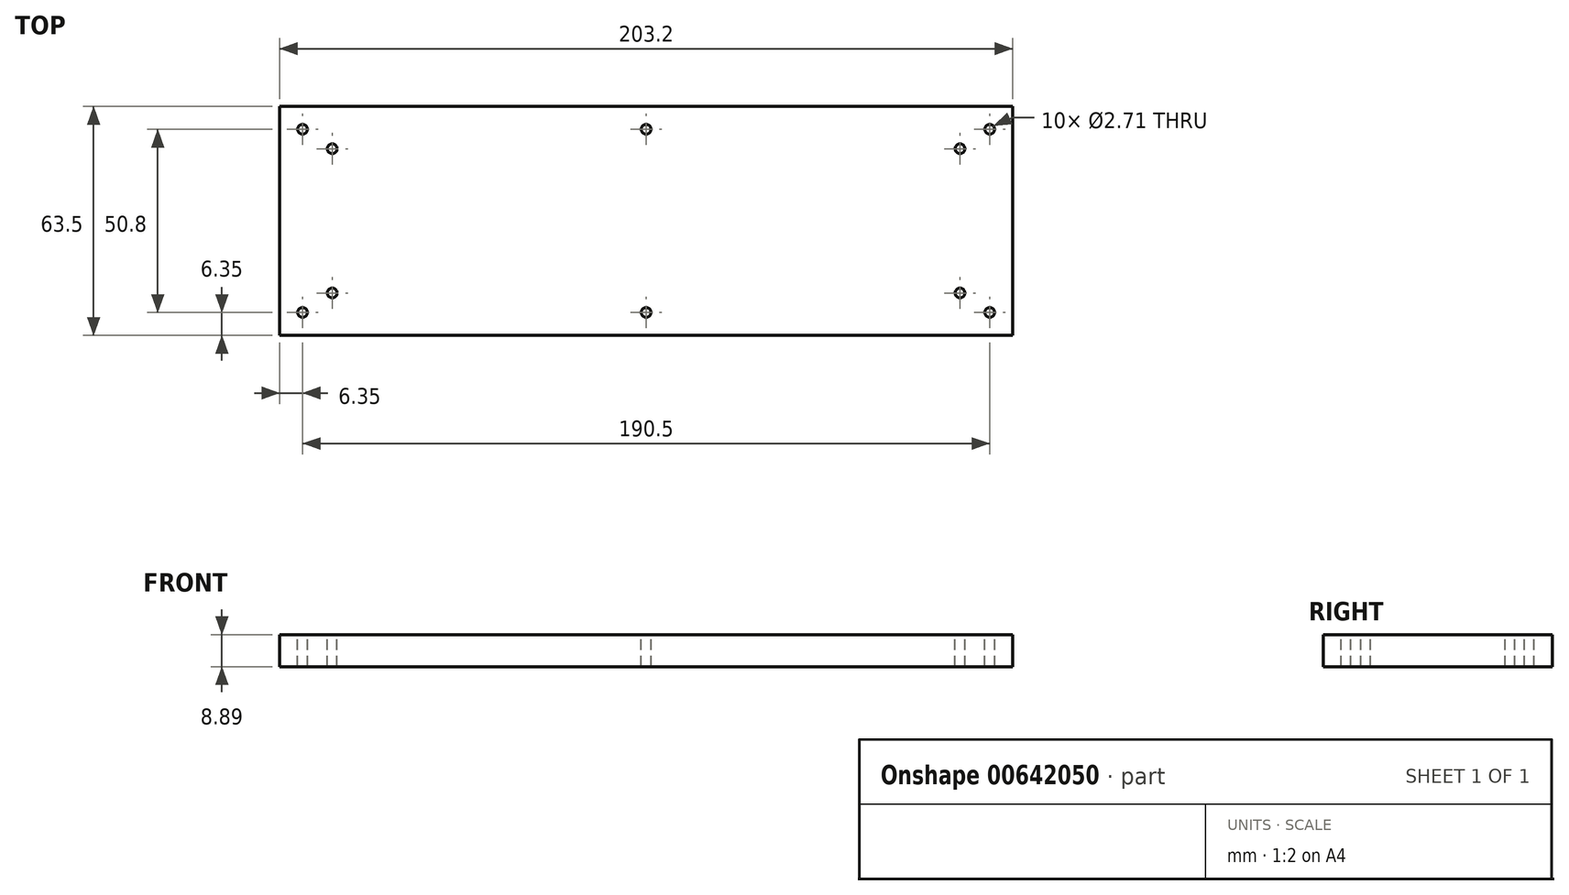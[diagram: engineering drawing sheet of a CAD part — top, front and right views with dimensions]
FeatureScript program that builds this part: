
annotation { "Feature Type Name" : "Feature", "Feature Type Description" : "" }
export const myFeature = defineFeature(function(context is Context, id is Id, definition is map)
    precondition{}
    {
        {
            var Q0;
            Q0=qCreatedBy(makeId("Top.planeOp"),FACE);
            var sketch = newSketch(context, id + "F0", { "sketchPlane" : qUnion([Q0])});
            skLineSegment(sketch, "E0.bottom", {"start": v(0, 0) * mm, "end": v(203.2, 0) * mm});
            skLineSegment(sketch, "E0.top", {"start": v(0, 63.5) * mm, "end": v(203.2, 63.5) * mm});
            skLineSegment(sketch, "E0.left", {"start": v(0, 0) * mm, "end": v(0, 63.5) * mm});
            skLineSegment(sketch, "E0.right", {"start": v(203.2, 0) * mm, "end": v(203.2, 63.5) * mm});
            skSolve(sketch);
        }
        {
            var Q0;
            Q0 = qSketchRegion(id + "F0", true);
            extrude(context, id + "F1", {"entities" : qUnion([Q0]), "depth" : 8.9 * mm, "offsetDistance" : 25.4 * mm});
        }
        {
            var Q0;
            Q0=makeQuery(id+"F1.opExtrude","CAP_FACE",FACE,{"disambiguationData":[OSD([sQuery(id+"F0.wireOp",EDGE,"E0.bottom"),sQuery(id+"F0.wireOp",EDGE,"E0.top"),sQuery(id+"F0.wireOp",EDGE,"E0.left"),sQuery(id+"F0.wireOp",EDGE,"E0.right")])],"isStart":false});
            var sketch = newSketch(context, id + "F2", { "sketchPlane" : qUnion([Q0])});
            skPoint(sketch, "E1", {"position": v(14.6, 51.75) * mm});
            skPoint(sketch, "E2", {"position": v(14.6, 11.75) * mm});
            skPoint(sketch, "E3", {"position": v(188.6, 51.75) * mm});
            skPoint(sketch, "E4", {"position": v(188.6, 11.75) * mm});
            skLineSegment(sketch, "E5", {"start": v(0, 31.75) * mm, "end": v(203.2, 31.75) * mm, "construction": true});
            skPoint(sketch, "E5.endSnap0", {"position": v(0, 31.75) * mm});
            skLineSegment(sketch, "E6", {"start": v(101.6, 63.5) * mm, "end": v(101.6, 0) * mm, "construction": true});
            skPoint(sketch, "E7", {"position": v(6.35, 57.15) * mm});
            skPoint(sketch, "E8", {"position": v(196.85, 57.15) * mm});
            skPoint(sketch, "E9", {"position": v(196.85, 6.35) * mm});
            skPoint(sketch, "E10", {"position": v(6.35, 6.35) * mm});
            skPoint(sketch, "E11", {"position": v(101.6, 57.15) * mm});
            skPoint(sketch, "E12", {"position": v(101.6, 6.35) * mm});
            skSolve(sketch);
        }
        {
            var Q0;
            Q0=sQuery(id+"F2.wireOp",VERTEX,"E8");
            var Q1;
            Q1=sQuery(id+"F2.wireOp",VERTEX,"E3");
            var Q2;
            Q2=sQuery(id+"F2.wireOp",VERTEX,"E4");
            var Q3;
            Q3=sQuery(id+"F2.wireOp",VERTEX,"E9");
            var Q4;
            Q4=sQuery(id+"F2.wireOp",VERTEX,"E10");
            var Q5;
            Q5=sQuery(id+"F2.wireOp",VERTEX,"E2");
            var Q6;
            Q6=sQuery(id+"F2.wireOp",VERTEX,"E1");
            var Q7;
            Q7=sQuery(id+"F2.wireOp",VERTEX,"E7");
            var Q8;
            Q8=sQuery(id+"F2.wireOp",VERTEX,"E11");
            var Q9;
            Q9=sQuery(id+"F2.wireOp",VERTEX,"E12");
            var Q10;
            Q10=makeQuery(id+"F1.opExtrude","SWEPT_BODY",BODY,{"disambiguationData":[OSD([sQuery(id+"F0.wireOp",EDGE,"E0.bottom"),sQuery(id+"F0.wireOp",EDGE,"E0.top"),sQuery(id+"F0.wireOp",EDGE,"E0.left"),sQuery(id+"F0.wireOp",EDGE,"E0.right")])]});
            hole(context, id + "F3", {"style" : HoleStyle.SIMPLE, "endStyle" : HoleEndStyle.THROUGH, "standardTappedOrClearance" : lookupTablePath({ "standard" : "ANSI", "engagement" : "75%", "pitch" : "32 tpi", "size" : "#6", "type" : "Tapped" }), "standardBlindInLast" : lookupTablePath({ "standard" : "ANSI", "engagement" : "75%", "pitch" : "32 tpi", "size" : "#6", "type" : "Tapped" }), "holeDiameter" : 2.7 * mm, "majorDiameter" : 3.5 * mm, "showTappedDepth" : true, "isTappedThrough" : true, "tappedDepth" : 10.32 * mm, "tapClearance" : 3, "startFromSketch" : true, "locations" : qUnion([Q0, Q1, Q2, Q3, Q4, Q5, Q6, Q7, Q8, Q9]), "scope" : qUnion([Q10])});
        }
    });
